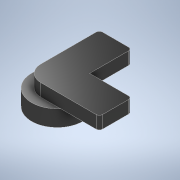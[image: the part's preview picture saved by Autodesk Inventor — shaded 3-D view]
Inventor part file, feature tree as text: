
AUTODESK INVENTOR PART (.ipt)
format: ipt  version: 2021 (Build 250183000, 183)  size: 125,440 bytes
history: native  units: mm
features: extrude x2, sketch x2
ambient origin geometry x8: Origin, YZ Plane, XZ Plane, XY Plane, X Axis, Y Axis, Z Axis, Center Point
bodies: Solid1 (feature_tree)
feature tree (4):
  extrude  "Extrusion1"  Depth=10.0mm TaperAngle=0.0deg
  extrude  "Extrusion2"  Depth=7.8mm
  sketch  "Sketch1"  dims[d0=31.5mm d1=10.0mm d2=0.0mm]
  sketch  "Sketch2"  dims[d3=20.0mm d4=36.0mm d5=36.0mm d6=2.0mm d7=20.0mm d8=20.0mm d9=7.8mm d10=0.0mm]
